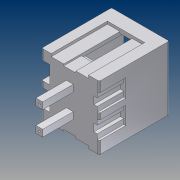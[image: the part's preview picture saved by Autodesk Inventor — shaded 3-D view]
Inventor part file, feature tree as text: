
AUTODESK INVENTOR PART (.ipt)
format: ipt  version: 2012 (Build 160160000, 160)  size: 219,648 bytes
history: native  units: mm (DEFAULTED — no unit token found)
features: extrude x15, sketch x15, pattern_linear x4
ambient origin geometry x8: Origin, YZ Plane, XZ Plane, XY Plane, X Axis, Y Axis, Z Axis, Center Point
bodies: Solid1 (feature_tree)
feature tree (34):
  extrude  "Extrusion1"  Depth=7.5mm TaperAngle=0.0deg
  extrude  "Extrusion2"  Depth=7.7mm TaperAngle=0.0deg
  extrude  "Extrusion3"  Depth=6.0mm TaperAngle=0.0deg
  extrude  "Extrusion4"  Depth=20.0mm TaperAngle=0.0deg
  extrude  "Extrusion5"  Depth=20.0mm TaperAngle=0.0deg
  extrude  "Extrusion6"  Depth=20.0mm TaperAngle=0.0deg
  extrude  "Extrusion7"  Depth=8.3mm TaperAngle=0.0deg
  pattern_linear  "Rectangular Pattern1"  Count1=2 Spacing1=3.5mm
  extrude  "Extrusion8"  Depth=3.9mm TaperAngle=0.0deg
  pattern_linear  "Rectangular Pattern2"  [2 undecoded]
  extrude  "Extrusion9"  [1 undecoded]
  pattern_linear  "Rectangular Pattern3"  [2 undecoded]
  extrude  "Extrusion10"  [1 undecoded]
  extrude  "Extrusion11"  [1 undecoded]
  extrude  "Extrusion12"  [1 undecoded]
  pattern_linear  "Rectangular Pattern4"  [2 undecoded]
  extrude  "Extrusion13"  [1 undecoded]
  extrude  "Extrusion14"  [1 undecoded]
  extrude  "Extrusion15"  [1 undecoded]
  sketch  "Skizze_1"  dims[d0=9.4mm d1=0.0mm d2=7.5mm d3=0.0mm]
  sketch  "Skizze_2"  dims[d4=7.7mm d5=0.0mm d6=7.7mm d7=0.0mm]
  sketch  "Skizze_3"  dims[d8=6.0mm d9=0.0mm d10=6.0mm d11=0.0mm]
  sketch  "Skizze_4"  dims[d12=3.6mm d13=0.0mm d14=20.0mm d16=3.5mm d17=10.0mm d19=0.0mm]
  sketch  "Skizze_5"  dims[d20=9.3mm d21=0.0mm d22=20.0mm d24=3.5mm d25=10.0mm d27=0.0mm]
  sketch  "Skizze_6"  dims[d28=4.5mm d29=0.0mm d30=20.0mm d32=3.5mm d33=10.0mm d35=0.0mm]
  sketch  "Skizze_7"  dims[d36=8.3mm d37=0.0mm d38=8.3mm d39=0.0mm]
  sketch  "Skizze_9"  dims[d40=9.15mm d41=0.0mm d42=20.0mm d44=3.5mm d45=10.0mm d47=0.0mm]
  sketch  "Skizze_11"  dims[d48=3.9mm d49=0.0mm d50=3.9mm d51=0.0mm]
  sketch  "Skizze_13"  dims[d52=0.254mm]
  sketch  "Skizze_14"  dims[d53=0.254mm d54=0.0mm]
  sketch  "Skizze_15"
  sketch  "Skizze_17"
  sketch  "Skizze_18"
  sketch  "Sketch15"
note: 13 required parameter values undecoded (feature->parameter linkage not recoverable at this tier; creation-order binding heuristic only, values carry confidence <= 0.55)
